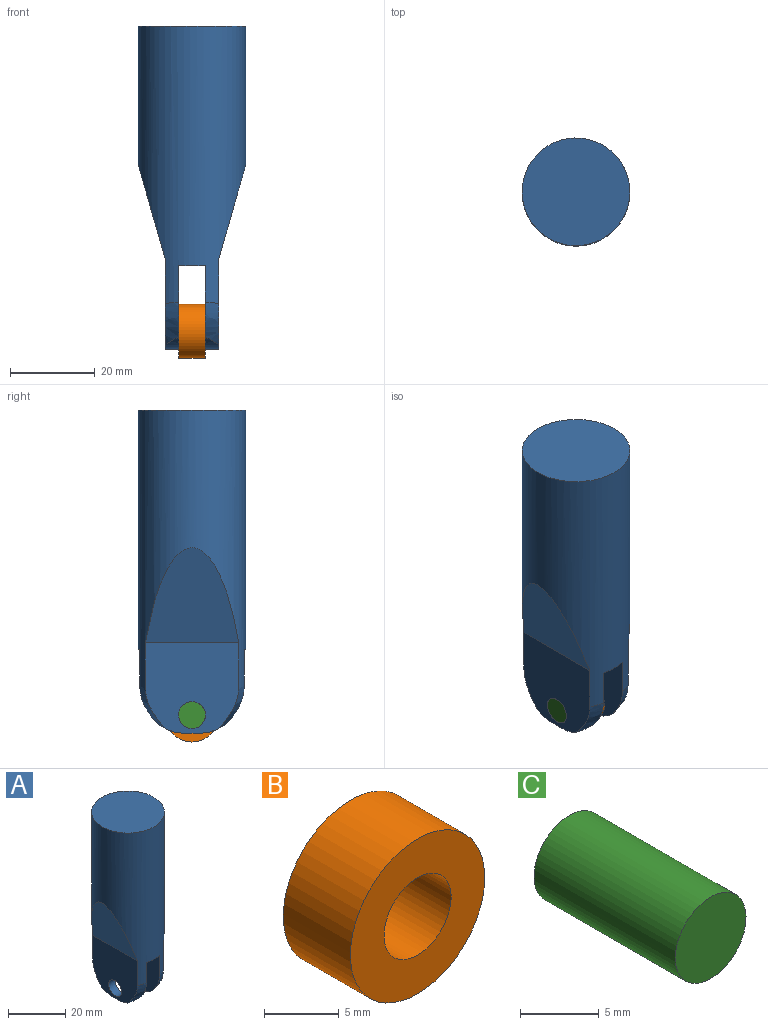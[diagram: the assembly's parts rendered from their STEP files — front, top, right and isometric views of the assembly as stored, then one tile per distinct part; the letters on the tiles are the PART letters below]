
ASSEMBLY  parts=3 mates=2
PART A: 21 faces, bbox 29.8x25.4x77.4 mm
  f0: cylinder r=12.7mm len=65.41mm, axis (0,0,-1), area 3763.7mm2, adj f3,f5,f7,f8,f9,f10,f12,f14
  f1: plane 3.32x3.18mm, normal (0,0,-1), area 10.5mm2, adj f2,f4,f7,f17
  f2: cylinder r=10.16mm len=7.15mm, axis (-1,0,0), area 20.2mm2, adj f1,f3,f7,f17
  f3: bspline ~16.51x14.68mm, area 33.3mm2, adj f0,f2,f7,f17
  f4: cylinder r=10.16mm len=7.15mm, axis (1,0,0), area 20.2mm2, adj f1,f5,f7,f17
  f5: bspline ~16.51x14.68mm, area 33.3mm2, adj f0,f4,f7,f17
  f6: plane 3.32x3.18mm, normal (0,0,-1), area 10.5mm2, adj f8,f11,f13,f16
  f7: plane 22x21.33mm, normal (1,0,0), area 392.8mm2, adj f0,f1,f2,f3,f4,f5,f9,f18
  f8: plane 22x21.33mm, normal (-1,0,0), area 392.8mm2, adj f0,f6,f10,f11,f12,f13,f14,f19
  f9: plane 22.37x22mm, normal (0.96,0,-0.27), area 362.8mm2, adj f0,f7
  f10: plane 22.37x22mm, normal (-0.96,0,-0.27), area 362.8mm2, adj f0,f8
  f11: cylinder r=10.16mm len=7.15mm, axis (-1,0,0), area 20.2mm2, adj f6,f8,f12,f16
  f12: bspline ~16.51x14.68mm, area 33.3mm2, adj f0,f8,f11,f16
  f13: cylinder r=10.16mm len=7.15mm, axis (1,0,0), area 20.2mm2, adj f6,f8,f14,f16
  f14: bspline ~16.51x14.68mm, area 33.3mm2, adj f0,f8,f13,f16
  f15: plane 25.4x6.35mm, normal (0,0,-1), area 159.6mm2, adj f0,f16,f17
  f16: plane 24.59x19.71mm, normal (1,0,0), area 400.6mm2, adj f0,f6,f11,f12,f13,f14,f15,f19
  f17: plane 24.59x19.71mm, normal (-1,0,0), area 400.6mm2, adj f0,f1,f2,f3,f4,f5,f15,f18
  f18: cylinder r=3.17mm len=6.35mm, axis (1,0,0), area 63.3mm2, adj f7,f17
  f19: cylinder r=3.17mm len=6.35mm, axis (1,0,0), area 63.3mm2, adj f8,f16
  f20: plane 25.4x25.4mm, normal (0,0,1), area 506.7mm2, adj f0
PART B: 4 faces, bbox 12.7x6.4x12.7 mm
  f0: cylinder r=6.35mm len=12.7mm, axis (0,1,0), area 253.4mm2, adj f1,f2
  f1: plane 12.7x12.7mm, normal (0,-1,0), area 95mm2, adj f0,f3
  f2: plane 12.7x12.7mm, normal (0,1,0), area 95mm2, adj f0,f3
  f3: cylinder r=3.17mm len=6.35mm, axis (0,-1,0), area 126.7mm2, adj f1,f2
PART C: 3 faces, bbox 6.4x12.7x6.4 mm
  f0: cylinder r=3.17mm len=12.7mm, axis (0,1,0), area 253.4mm2, adj f1,f2
  f1: plane 6.35x6.35mm, normal (0,-1,0), area 31.7mm2, adj f0
  f2: plane 6.35x6.35mm, normal (0,1,0), area 31.7mm2, adj f0
PLACE A t=(-28.12,-15.48,-48.02)mm
PLACE B rot(axis=(0,0,-1),90deg) t=(-24.95,-15.48,-43.75)mm
PLACE C rot(axis=(-0.58,0.58,0.58),120deg) t=(-34.47,-15.48,-43.75)mm
MATE fastened C.f0 <-> A.f18  axis (1,0,0) through (-21.77,-15.48,-43.75)mm
MATE revolute B.f3 <-> C.f0  axis (-1,0,0) through (-28.12,-15.48,-43.75)mm
